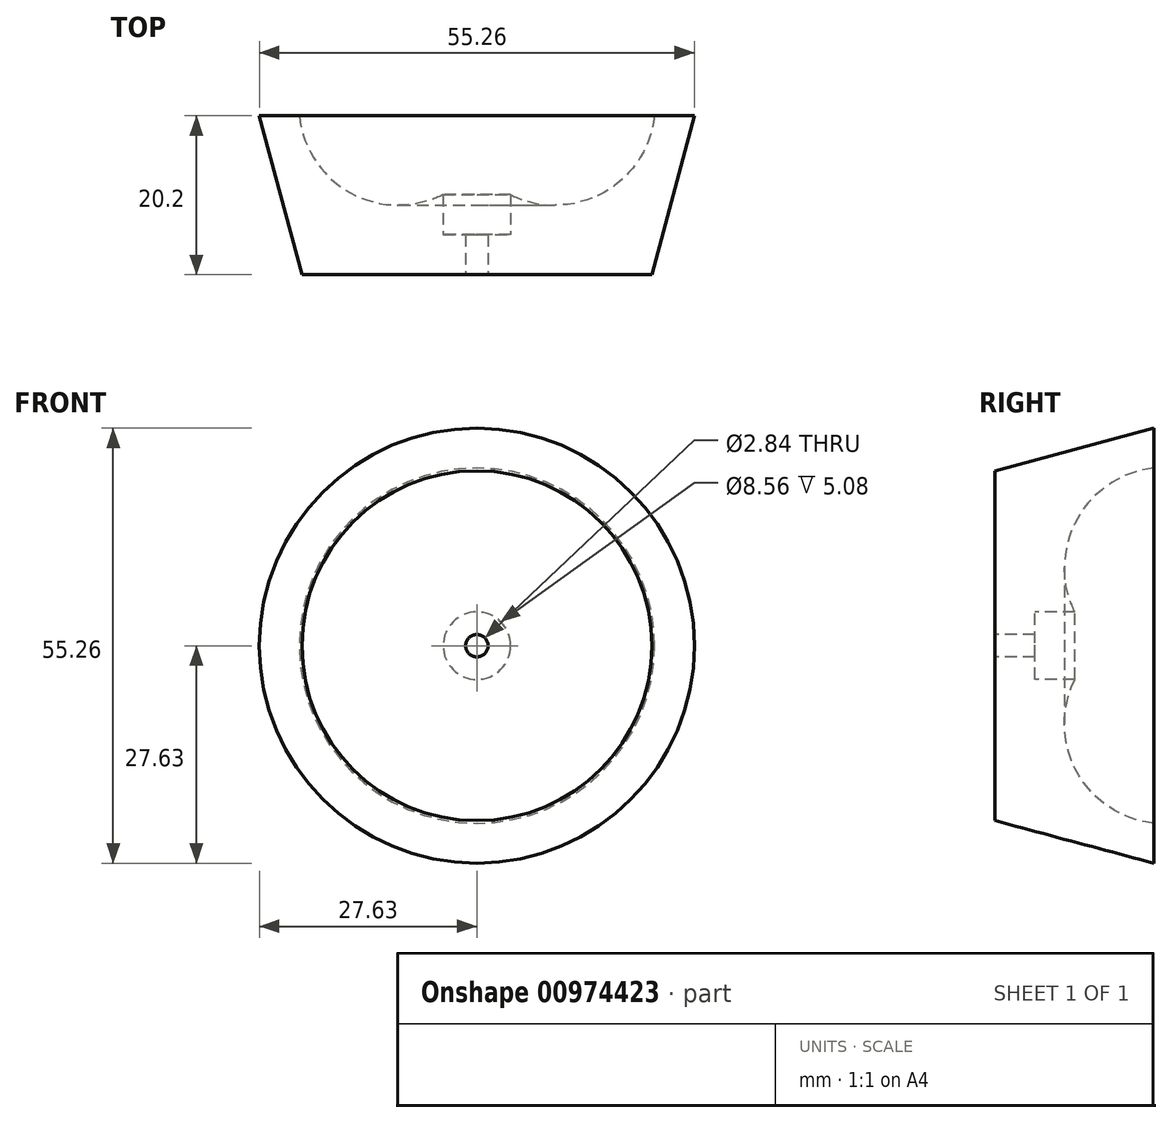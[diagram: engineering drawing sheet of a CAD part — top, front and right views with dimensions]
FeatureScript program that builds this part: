
annotation { "Feature Type Name" : "Feature", "Feature Type Description" : "" }
export const myFeature = defineFeature(function(context is Context, id is Id, definition is map)
    precondition{}
    {
        {
            var Q0;
            Q0=qCreatedBy(makeId("Top.planeOp"),FACE);
            var sketch = newSketch(context, id + "F0", { "sketchPlane" : qUnion([Q0])});
            skLineSegment(sketch, "E0", {"start": v(-4.28, -7.22) * mm, "end": v(-4.28, -2.14) * mm});
            skLineSegment(sketch, "E1", {"start": v(-27.63, 7.9) * mm, "end": v(-22.55, 7.9) * mm});
            skArc(sketch, "E2", {"start": v(-22.55, 7.9) * mm, "mid": v(-16.04, -1.9) * mm, "end": v(-4.28, -2.14) * mm});
            skLineSegment(sketch, "E3", {"start": v(-4.28, -7.22) * mm, "end": v(-1.42, -7.22) * mm});
            skLineSegment(sketch, "E4", {"start": v(-1.42, -7.22) * mm, "end": v(-1.42, -12.3) * mm});
            skLineSegment(sketch, "E5", {"start": v(-1.42, -12.3) * mm, "end": v(-22.22, -12.3) * mm});
            skLineSegment(sketch, "E6", {"start": v(-27.63, 7.9) * mm, "end": v(-22.22, -12.3) * mm});
            skLineSegment(sketch, "E7", {"start": v(0, -12.29) * mm, "end": v(0, 18.2) * mm, "construction": true});
            skLineSegment(sketch, "E8", {"start": v(-1.42, -12.3) * mm, "end": v(0, -12.29) * mm, "construction": true});
            skSolve(sketch);
        }
        {
            var Q0;
            Q0 = qSketchRegion(id + "F0", true);
            var Q1;
            Q1=sQuery(id+"F0.wireOp",EDGE,"E7");
            revolve(context, id + "F1", {"surfaceOperationType" : NewSurfaceOperationType.NEW, "entities" : qUnion([Q0]), "axis" : qUnion([Q1]), "revolveType" : RevolveType.FULL});
        }
    });
